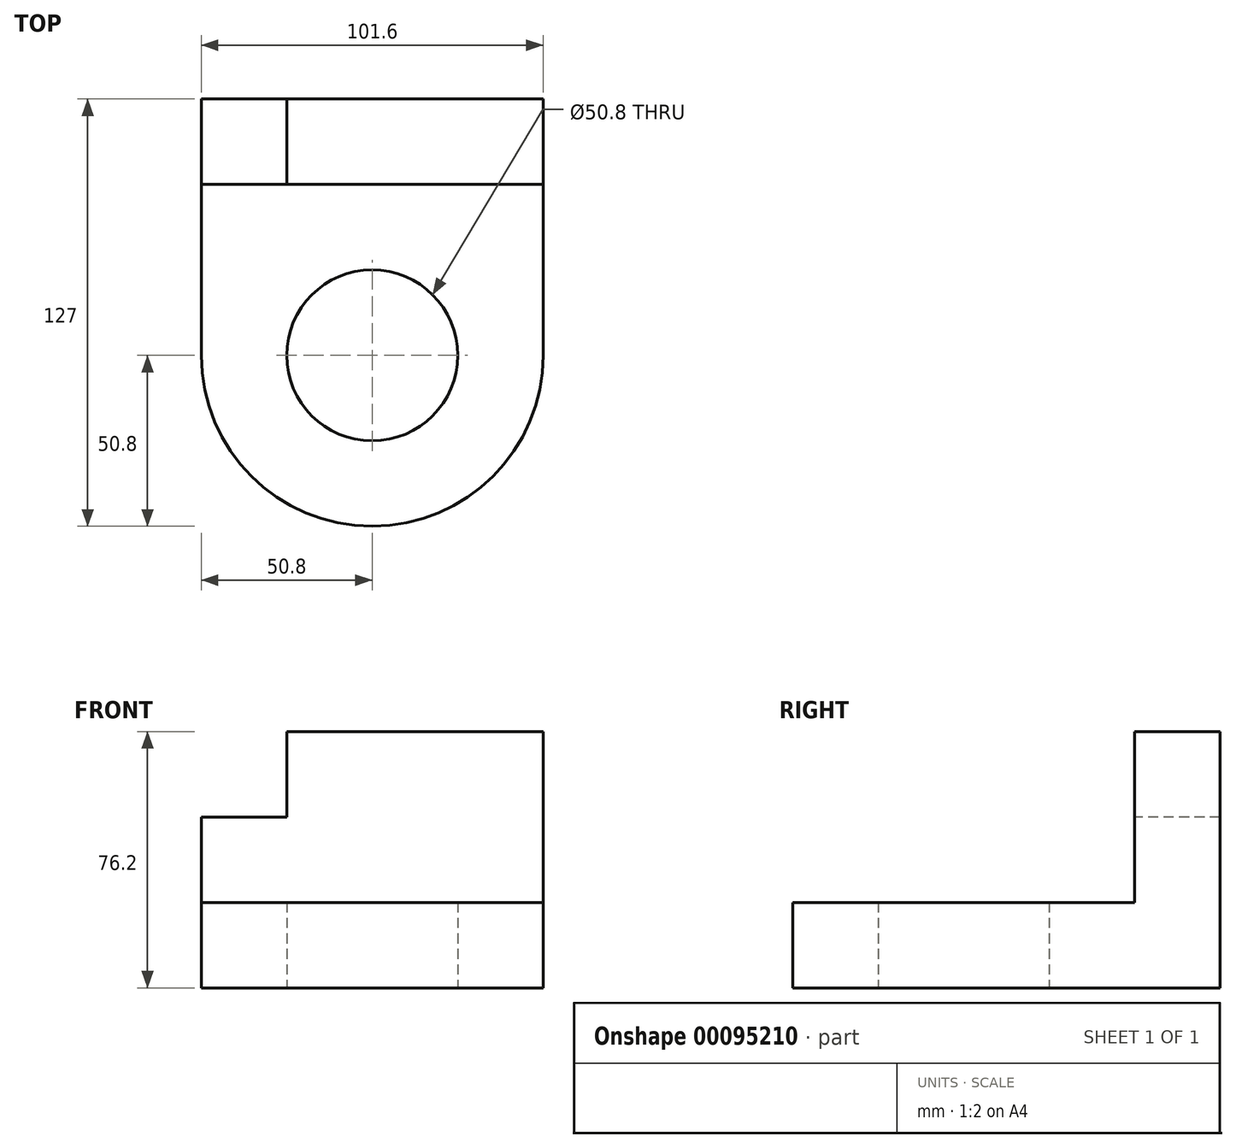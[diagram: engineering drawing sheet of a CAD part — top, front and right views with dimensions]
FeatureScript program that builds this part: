
annotation { "Feature Type Name" : "Feature", "Feature Type Description" : "" }
export const myFeature = defineFeature(function(context is Context, id is Id, definition is map)
    precondition{}
    {
        {
            var Q0;
            Q0=qCreatedBy(makeId("Top.planeOp"),FACE);
            var sketch = newSketch(context, id + "F0", { "sketchPlane" : qUnion([Q0])});
            skLineSegment(sketch, "E0.bottom", {"start": v(50.8, -38.1) * mm, "end": v(-50.8, -38.1) * mm});
            skLineSegment(sketch, "E0.top", {"start": v(50.8, 38.1) * mm, "end": v(-50.8, 38.1) * mm});
            skLineSegment(sketch, "E0.left", {"start": v(50.8, -38.1) * mm, "end": v(50.8, 38.1) * mm});
            skLineSegment(sketch, "E0.right", {"start": v(-50.8, -38.1) * mm, "end": v(-50.8, 38.1) * mm});
            skPoint(sketch, "E0.middle", {"position": v(0, 0) * mm});
            skCircle(sketch, "E1", {"center": v(0, -38.1) * mm, "radius": 50.8 * mm});
            skCircle(sketch, "E2", {"center": v(0, -38.1) * mm, "radius": 25.4 * mm});
            skPoint(sketch, "E3", {"position": v(0, -88.9) * mm});
            skSolve(sketch);
        }
        {
            var Q0;
            Q0 = qSketchRegion(id + "F0", true);
            extrude(context, id + "F1", {"entities" : qUnion([Q0]), "depth" : 25.4 * mm});
        }
        {
            var Q0;
            Q0=makeQuery(id+"F1.opExtrude","CAP_FACE",FACE,{"disambiguationData":[OSD([sQuery(id+"F0.wireOp",EDGE,"E0.top"),sQuery(id+"F0.wireOp",EDGE,"E0.left"),sQuery(id+"F0.wireOp",EDGE,"E0.right"),sQuery(id+"F0.wireOp",EDGE,"E1"),sQuery(id+"F0.wireOp",EDGE,"E2")])],"isStart":false});
            var sketch = newSketch(context, id + "F2", { "sketchPlane" : qUnion([Q0])});
            skLineSegment(sketch, "E4.bottom", {"start": v(-50.8, 38.1) * mm, "end": v(50.8, 38.1) * mm});
            skLineSegment(sketch, "E4.top", {"start": v(-50.8, 12.7) * mm, "end": v(50.8, 12.7) * mm});
            skLineSegment(sketch, "E4.left", {"start": v(-50.8, 38.1) * mm, "end": v(-50.8, 12.7) * mm});
            skLineSegment(sketch, "E4.right", {"start": v(50.8, 38.1) * mm, "end": v(50.8, 12.7) * mm});
            skSolve(sketch);
        }
        {
            var Q0;
            Q0 = qSketchRegion(id + "F2", true);
            extrude(context, id + "F3", {"entities" : qUnion([Q0]), "operationType" : NewBodyOperationType.ADD, "depth" : 50.8 * mm});
        }
        {
            var Q0;
            Q0=makeQuery(id+"F3.opExtrude","SWEPT_FACE",FACE,{"disambiguationData":[OSD([sQuery(id+"F2.wireOp",EDGE,"E4.top")])]});
            var sketch = newSketch(context, id + "F4", { "sketchPlane" : qUnion([Q0])});
            skLineSegment(sketch, "E5.bottom", {"start": v(-50.8, 76.2) * mm, "end": v(-25.4, 76.2) * mm});
            skLineSegment(sketch, "E5.top", {"start": v(-50.8, 50.8) * mm, "end": v(-25.4, 50.8) * mm});
            skLineSegment(sketch, "E5.left", {"start": v(-50.8, 76.2) * mm, "end": v(-50.8, 50.8) * mm});
            skLineSegment(sketch, "E5.right", {"start": v(-25.4, 76.2) * mm, "end": v(-25.4, 50.8) * mm});
            skSolve(sketch);
        }
        {
            var Q0;
            Q0 = qSketchRegion(id + "F4", true);
            extrude(context, id + "F5", {"entities" : qUnion([Q0]), "operationType" : NewBodyOperationType.REMOVE, "endBound" : BoundingType.THROUGH_ALL, "oppositeDirection" : true, "depth" : 25.4 * mm});
        }
    });
